# Revit family: Panneau de brassage
name_source: partatom
category: Equipement spécialisé
units: mm (PartAtom-declared; Revit-internal decimal feet)

## family parameters
Basée sur le plan de construction = Non
Cote de connecteur circulaire = Utiliser le diamètre
Couper avec des vides une fois chargée = Non
Partagée = Oui
Point de calcul de pièce = Non
Toujours verticalement = Oui
Type d'élément = Normal

## types (1)
- Panneau de brassage
    Blindé = Oui
    Classe ETIM = EC001128
    Couleur = IDS_NOIR
    Dimension modulaire = 19 pouces
    EAN = 3414972185509
    Elévation par défaut = 0 mm  [stored 0 ft]
    Fonction = Panneaux de brassage connecteurs cuivre
    Hauteur = 43.8 mm  [stored 0.143701 ft]
    IK = IK04
    Largeur (mm) = 482.6 mm
    Libellé BIM = Panneau 24 RJ45 Cat 5e 6 6A Keystone à équiper avec support de câble métal
    Lien e-catalogue = https://www.legrand.fr
    Nature du câble pour connexion = Souple
    Nombre d'unités en hauteur = 1
    Nombre de connecteurs = 24
    Profondeur = 140 mm  [stored 0.459318 ft]
    RAL = 9017
    Référence Legrand = 632850
    Température de fonctionnement = -10_à_60
    Température de stockage = -10_à_70
    Type de connecteur = RJ45

note: [stored X ft] marks values corroborated as IEEE doubles in the binary element streams (Revit-internal decimal feet)
